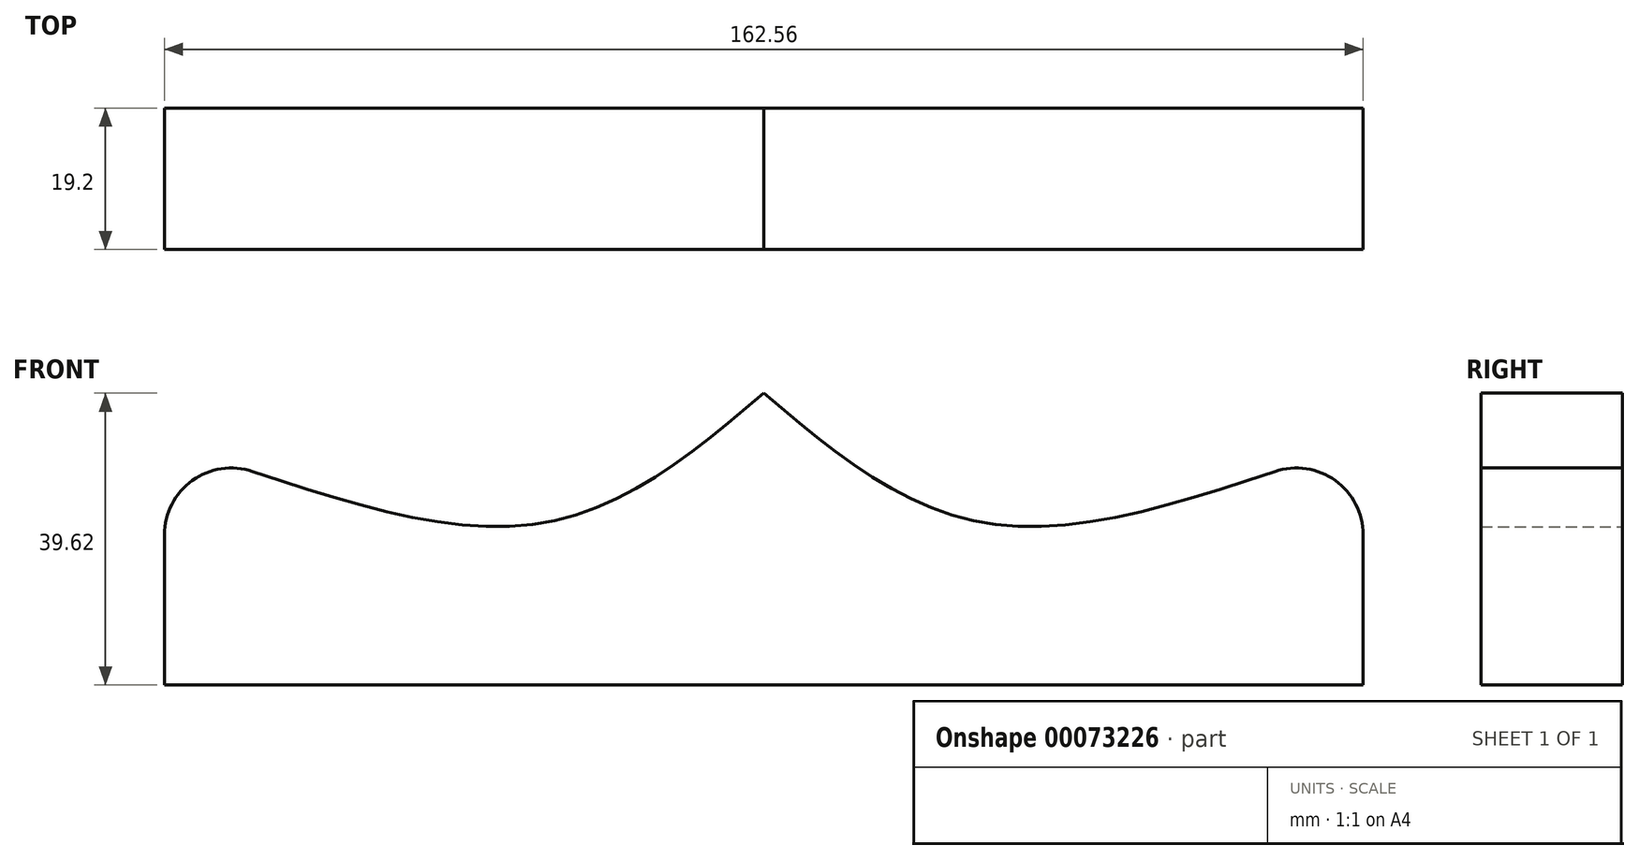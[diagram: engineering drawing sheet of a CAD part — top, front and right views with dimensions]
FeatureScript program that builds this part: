
annotation { "Feature Type Name" : "Feature", "Feature Type Description" : "" }
export const myFeature = defineFeature(function(context is Context, id is Id, definition is map)
    precondition{}
    {
        {
            var Q0;
            Q0=qCreatedBy(makeId("Front.planeOp"),FACE);
            var sketch = newSketch(context, id + "F0", { "sketchPlane" : qUnion([Q0])});
            skPoint(sketch, "E0", {"position": v(-81.28, 0) * mm});
            skPoint(sketch, "E1", {"position": v(81.28, 0) * mm});
            skLineSegment(sketch, "E2", {"start": v(0, 0) * mm, "end": v(81.28, 0) * mm});
            skLineSegment(sketch, "E3", {"start": v(81.28, 0) * mm, "end": v(-81.28, 0) * mm});
            skLineSegment(sketch, "E4", {"start": v(-81.28, 0) * mm, "end": v(-81.28, 20.4) * mm});
            skLineSegment(sketch, "E5", {"start": v(0, 0) * mm, "end": v(0, 39.62) * mm});
            skFitSpline(sketch, "E6", {"points": [v(-81.28, 32.99) * mm, v(-31.12, 21.83) * mm, v(0, 39.62) * mm], "startDerivative": vector(99.3, -32.25) * mm, "endDerivative": vector(62.74, 53.26) * mm});
            skArc(sketch, "E7.filletArc", {"start": v(-69.34, 29) * mm, "mid": v(-77.51, 27.76) * mm, "end": v(-81.28, 20.4) * mm});
            skFitSpline(sketch, "E8.MirrorCS", {"points": [v(81.28, 32.99) * mm, v(31.12, 21.83) * mm, v(0, 39.62) * mm], "startDerivative": vector(-99.3, -32.25) * mm, "endDerivative": vector(-62.74, 53.26) * mm});
            skArc(sketch, "E9.MirrorCS", {"start": v(69.34, 29) * mm, "mid": v(77.51, 27.76) * mm, "end": v(81.28, 20.4) * mm});
            skLineSegment(sketch, "E10.MirrorCS", {"start": v(81.28, 0) * mm, "end": v(81.28, 20.4) * mm});
            skPoint(sketch, "E11", {"position": v(-72.22, 29.46) * mm});
            skPoint(sketch, "E12", {"position": v(72.22, 29.46) * mm});
            skSolve(sketch);
        }
        {
            var Q0;
            {var subQ0=sQuery(id+"F0.wireOp",EDGE,"E5");Q0=makeQuery(id+"F0.imprint","IMPRINT",FACE,{"disambiguationData":[TD([[makeQuery(id+"F0.imprint","IMPRINT",EDGE,{"derivedFrom":subQ0}),-1.0]])]});}
            var Q1;
            {var subQ1=sQuery(id+"F0.wireOp",EDGE,"E4");Q1=makeQuery(id+"F0.imprint","IMPRINT",FACE,{"disambiguationData":[TD([[makeQuery(id+"F0.imprint","IMPRINT",EDGE,{"derivedFrom":subQ1}),-1.0]])]});}
            extrude(context, id + "F1", {"entities" : qUnion([Q0, Q1]), "depth" : 19.2 * mm});
        }
    });
